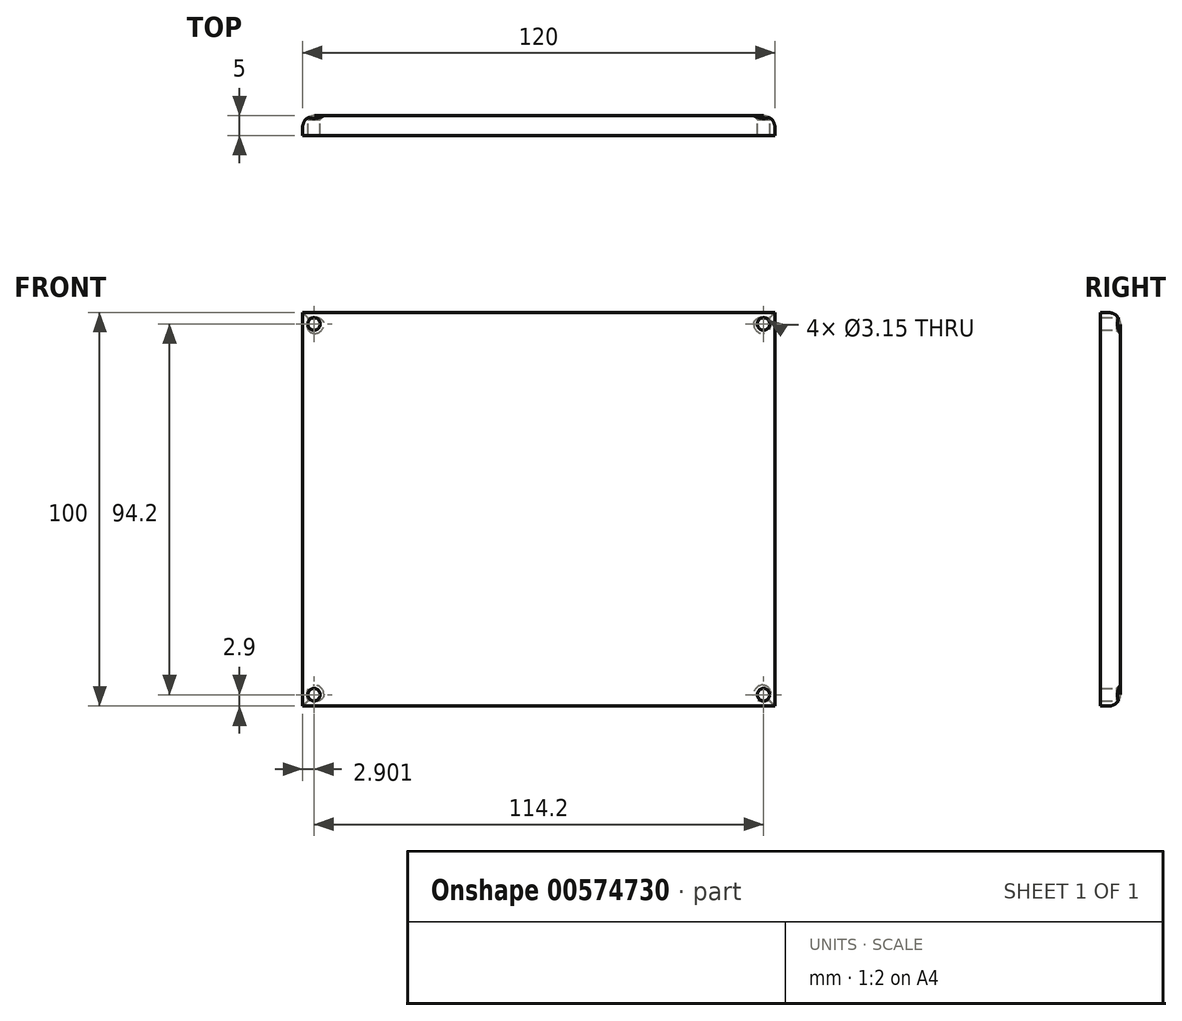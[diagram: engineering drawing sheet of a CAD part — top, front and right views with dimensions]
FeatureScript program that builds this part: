
annotation { "Feature Type Name" : "Feature", "Feature Type Description" : "" }
export const myFeature = defineFeature(function(context is Context, id is Id, definition is map)
    precondition{}
    {
        {
            var Q0;
            Q0=qCreatedBy(makeId("Front.planeOp"),FACE);
            var sketch = newSketch(context, id + "F0", { "sketchPlane" : qUnion([Q0])});
            skLineSegment(sketch, "E0.bottom", {"start": v(-60.3, 50) * mm, "end": v(59.7, 50) * mm});
            skLineSegment(sketch, "E0.top", {"start": v(-60.3, -50) * mm, "end": v(60.3, -50) * mm});
            skLineSegment(sketch, "E0.left", {"start": v(-60.3, 50) * mm, "end": v(-60.3, -50) * mm});
            skLineSegment(sketch, "E0.right", {"start": v(59.7, 50) * mm, "end": v(59.7, -50) * mm});
            skLineSegment(sketch, "E1", {"start": v(-60.3, 50) * mm, "end": v(60.3, -50) * mm, "construction": true});
            skPoint(sketch, "E2", {"position": v(-57.4, 47.1) * mm});
            skPoint(sketch, "E3", {"position": v(56.8, 47.1) * mm});
            skPoint(sketch, "E4", {"position": v(56.8, -47.1) * mm});
            skPoint(sketch, "E5", {"position": v(-57.4, -47.1) * mm});
            skSolve(sketch);
        }
        {
            var Q0;
            Q0=makeQuery(id+"F0.imprint","IMPRINT",FACE,{"disambiguationData":[TD([[makeQuery(id+"F0.imprint","IMPRINT",EDGE,{"derivedFrom":sQuery(id+"F0.wireOp",EDGE,"E0.bottom")}),-1.0]])]});
            extrude(context, id + "F1", {"entities" : qUnion([Q0]), "depth" : 5 * mm, "offsetDistance" : 25 * mm});
        }
        {
            var Q0;
            Q0=sQuery(id+"F0.wireOp",VERTEX,"E2");
            var Q1;
            Q1=sQuery(id+"F0.wireOp",VERTEX,"E3");
            var Q2;
            Q2=sQuery(id+"F0.wireOp",VERTEX,"E4");
            var Q3;
            Q3=sQuery(id+"F0.wireOp",VERTEX,"E5");
            var Q4;
            Q4=makeQuery(id+"F1.opExtrude","SWEPT_BODY",BODY,{"disambiguationData":[OSD([sQuery(id+"F0.wireOp",EDGE,"E0.bottom"),sQuery(id+"F0.wireOp",EDGE,"E0.top"),sQuery(id+"F0.wireOp",EDGE,"E0.left"),sQuery(id+"F0.wireOp",EDGE,"E0.right")])]});
            hole(context, id + "F2", {"style" : HoleStyle.C_SINK, "endStyle" : HoleEndStyle.THROUGH, "oppositeDirection" : true, "holeDiameter" : 3.15 * mm, "cSinkDiameter" : 5 * mm, "cSinkAngle" : 90 * degree, "isTappedThrough" : true, "tappedDepth" : 12 * mm, "tapClearance" : 3, "locations" : qUnion([Q0, Q1, Q2, Q3]), "scope" : qUnion([Q4])});
        }
        {
            var Q0;
            Q0=makeQuery(id+"F1.opExtrude","CAP_EDGE",EDGE,{"disambiguationData":[OSD([sQuery(id+"F0.wireOp",EDGE,"E0.top")])],"isStart":true});
            var Q1;
            Q1=makeQuery(id+"F1.opExtrude","CAP_EDGE",EDGE,{"disambiguationData":[OSD([sQuery(id+"F0.wireOp",EDGE,"E0.right")])],"isStart":true});
            var Q2;
            Q2=makeQuery(id+"F1.opExtrude","CAP_EDGE",EDGE,{"disambiguationData":[OSD([sQuery(id+"F0.wireOp",EDGE,"E0.left")])],"isStart":true});
            var Q3;
            Q3=makeQuery(id+"F1.opExtrude","CAP_EDGE",EDGE,{"disambiguationData":[OSD([sQuery(id+"F0.wireOp",EDGE,"E0.bottom")])],"isStart":true});
            fillet(context, id + "F3", {"entities" : qUnion([Q0, Q1, Q2, Q3]), "radius" : 3 * mm, "tangentPropagation" : true, "allowEdgeOverflow" : false});
        }
    });
